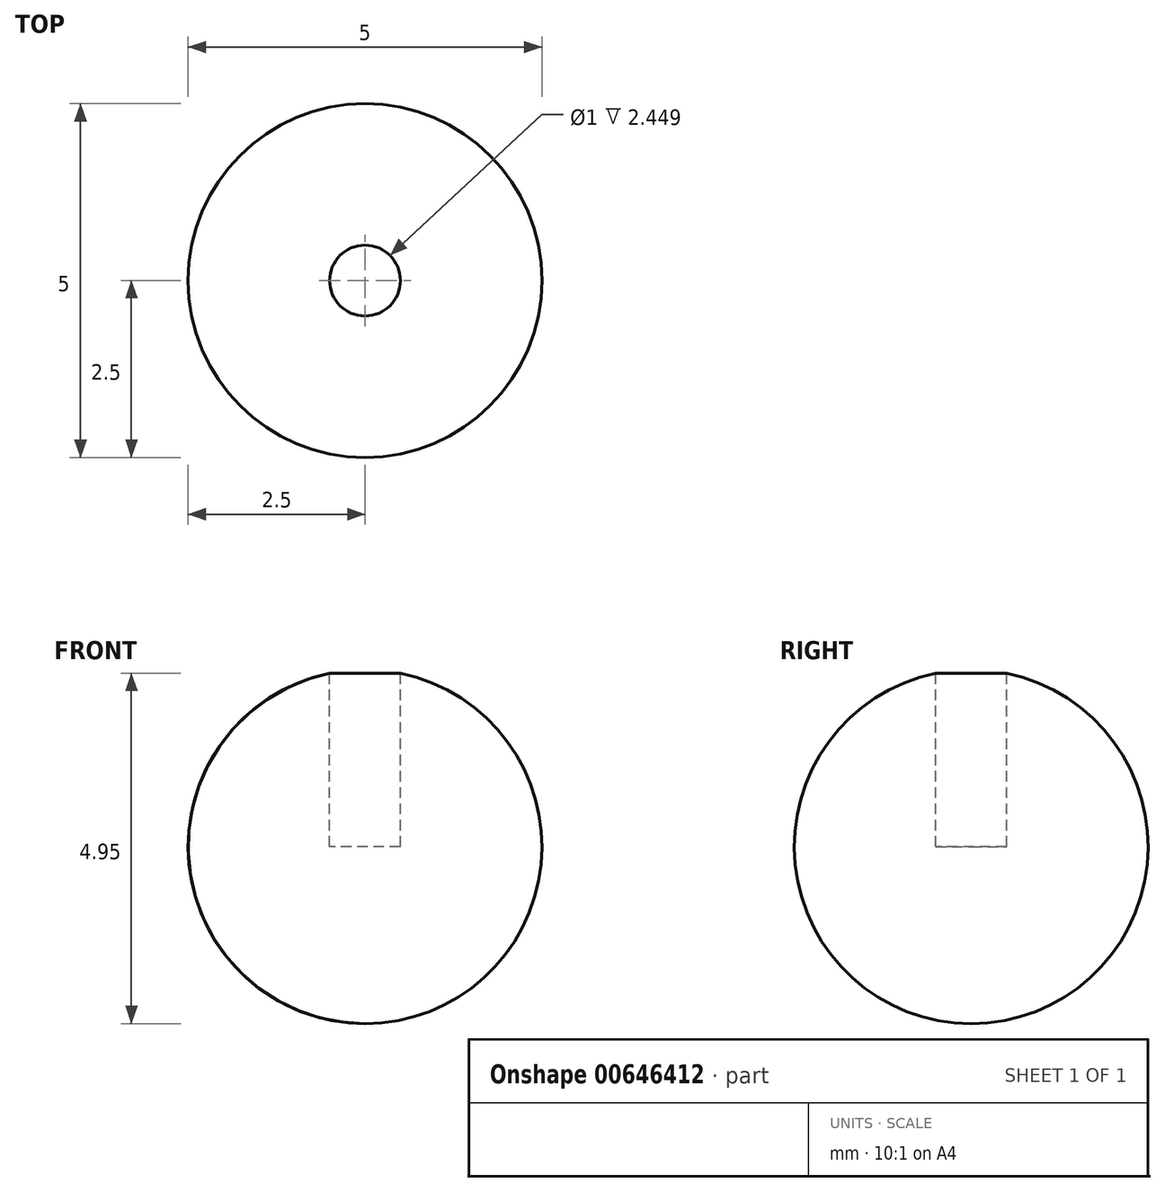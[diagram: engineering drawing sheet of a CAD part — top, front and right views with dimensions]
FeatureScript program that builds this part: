
annotation { "Feature Type Name" : "Feature", "Feature Type Description" : "" }
export const myFeature = defineFeature(function(context is Context, id is Id, definition is map)
    precondition{}
    {
        {
            var Q0;
            Q0=qCreatedBy(makeId("Front.planeOp"),FACE);
            var sketch = newSketch(context, id + "F0", { "sketchPlane" : qUnion([Q0])});
            skArc(sketch, "E0", {"start": v(-0.5, 2.45) * mm, "mid": v(-2.49, -0.25) * mm, "end": v(0, -2.5) * mm});
            skLineSegment(sketch, "E1.bottom", {"start": v(0, 0) * mm, "end": v(-0.5, 0) * mm});
            skLineSegment(sketch, "E1.right", {"start": v(-0.5, 0) * mm, "end": v(-0.5, 2.45) * mm});
            skLineSegment(sketch, "E2", {"start": v(0, 0) * mm, "end": v(0, -2.5) * mm});
            skPoint(sketch, "E3.orphan", {"position": v(0.5, 0) * mm});
            skSolve(sketch);
        }
        {
            var Q0;
            Q0=makeQuery(id+"F0.imprint","IMPRINT",FACE,{"disambiguationData":[TD([[makeQuery(id+"F0.imprint","IMPRINT",EDGE,{"derivedFrom":sQuery(id+"F0.wireOp",EDGE,"E0")}),1.0]])]});
            var Q1;
            Q1=sQuery(id+"F0.wireOp",EDGE,"E2");
            revolve(context, id + "F1", {"entities" : qUnion([Q0]), "axis" : qUnion([Q1]), "revolveType" : RevolveType.FULL});
        }
    });
